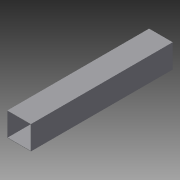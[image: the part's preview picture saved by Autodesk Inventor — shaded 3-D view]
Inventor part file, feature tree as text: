
AUTODESK INVENTOR PART (.ipt)
format: ipt  version: 2016 (Build 200138000, 138)  size: 75,776 bytes
history: native  units: in
note: dims shown in document units (in); Inventor stores cm internally (conversion verified against a paired STEP export)
features: extrude x1, sketch x1
ambient origin geometry x8: Origin, YZ Plane, XZ Plane, XY Plane, X Axis, Y Axis, Z Axis, Center Point
bodies: Solid1 (feature_tree)
feature tree (2):
  extrude  "Extrusion1"  Depth=2.0in
  sketch  "Sketch1"  dims[d0=2.0in d1=2.0in d2=0.03in d3=12.0in d4=0.0in]
